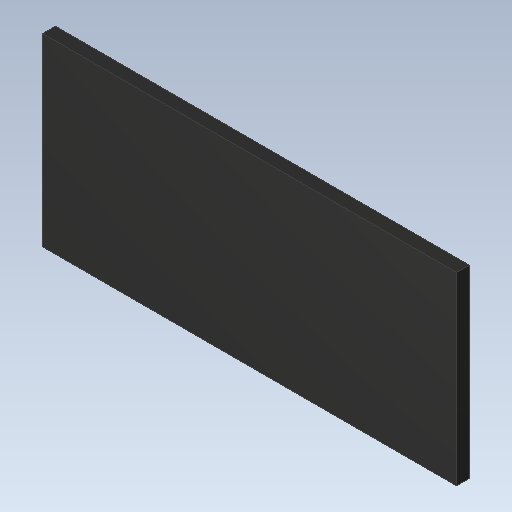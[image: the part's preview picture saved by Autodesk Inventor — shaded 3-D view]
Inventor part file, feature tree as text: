
AUTODESK INVENTOR PART (.ipt)
format: ipt  version: 2020 (Build 240168000, 168)  size: 86,016 bytes
history: imported  units: in
note: dims shown in document units (in); Inventor stores cm internally (conversion verified against a paired STEP export)
features: imported_body x1
ambient origin geometry x8: Origin, YZ Plane, XZ Plane, XY Plane, X Axis, Y Axis, Z Axis, Center Point
bodies: Solid1 (imported_parasolid), Body1 (imported_parasolid)
feature tree (1):
  imported_body  NMx_Import_Brep_tag  [imported B-rep: ~6 faces, bbox_mm=[3.2508, 1.4508, 0.1]]
